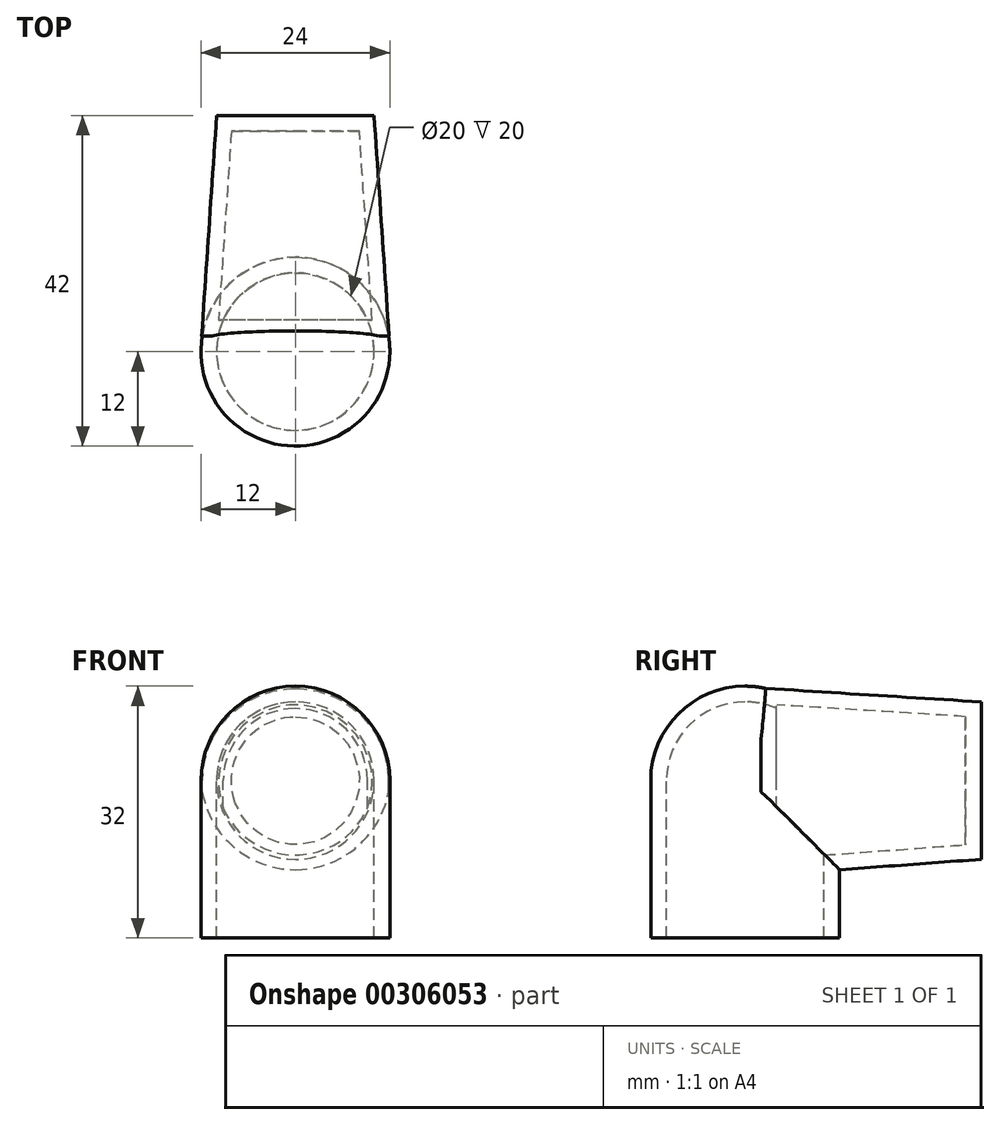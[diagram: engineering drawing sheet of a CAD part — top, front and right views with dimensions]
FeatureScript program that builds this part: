
annotation { "Feature Type Name" : "Feature", "Feature Type Description" : "" }
export const myFeature = defineFeature(function(context is Context, id is Id, definition is map)
    precondition{}
    {
        {
            var Q0;
            Q0=qCreatedBy(makeId("Front.planeOp"),FACE);
            cPlane(context, id + "F0", {"entities" : qUnion([Q0]), "cplaneType" : CPlaneType.OFFSET, "offset" : 28 * mm, "width" : 150 * mm, "height" : 150 * mm});
        }
        {
            var Q0;
            Q0=qCreatedBy(makeId("Front.planeOp"),FACE);
            var sketch = newSketch(context, id + "F1", { "sketchPlane" : qUnion([Q0])});
            skPoint(sketch, "E0", {"position": v(0, 12.5) * mm});
            skPoint(sketch, "E1", {"position": v(0, 27.5) * mm});
            skCircle(sketch, "E2", {"center": v(0, 20) * mm, "radius": 10 * mm});
            skSolve(sketch);
        }
        {
            var Q0;
            Q0=qCreatedBy(makeId("Top.planeOp"),FACE);
            var sketch = newSketch(context, id + "F2", { "sketchPlane" : qUnion([Q0])});
            skCircle(sketch, "E3", {"center": v(0, -30) * mm, "radius": 12 * mm});
            skPoint(sketch, "E4", {"position": v(0, -18) * mm});
            skPoint(sketch, "E5", {"position": v(0, -42) * mm});
            skSolve(sketch);
        }
        {
            var Q0;
            Q0=qCreatedBy(makeId("Right.planeOp"),FACE);
            var sketch = newSketch(context, id + "F3", { "sketchPlane" : qUnion([Q0])});
            skLineSegment(sketch, "E6", {"start": v(-30, 0) * mm, "end": v(-30, 20) * mm});
            skLineSegment(sketch, "E7", {"start": v(-42, 0) * mm, "end": v(-42, 20) * mm});
            skArc(sketch, "E8", {"start": v(-30, 32) * mm, "mid": v(-38.49, 28.49) * mm, "end": v(-42, 20) * mm});
            skLineSegment(sketch, "E9", {"start": v(-30, 32) * mm, "end": v(-30, 20) * mm});
            skLineSegment(sketch, "E10", {"start": v(-30, 0) * mm, "end": v(-42, 0) * mm});
            skSolve(sketch);
        }
        {
            var Q0;
            {var subQ0=sQuery(id+"F3.wireOp",EDGE,"E9");var subQ1=sQuery(id+"F3.wireOp",EDGE,"7151c649-8130-492b-bd59-bcbd0ac8ae9a");var subQ2=makeQuery(id+"F3.imprint","INTERSECT",VERTEX,{"derivedFrom":[subQ1,subQ0]});Q0=makeQuery(id+"F3.imprint","IMPRINT",FACE,{"disambiguationData":[TD([[makeQuery(id+"F3.imprint","IMPRINT",EDGE,{"disambiguationData":[TD([[subQ2,1.0]])],"derivedFrom":subQ1}),1.0]])]});}
            var Q1;
            {var subQ4=sQuery(id+"F3.wireOp",EDGE,"E6");Q1=makeQuery(id+"F3.imprint","IMPRINT",FACE,{"disambiguationData":[TD([[makeQuery(id+"F3.imprint","IMPRINT",EDGE,{"derivedFrom":subQ4}),1.0]])]});}
            var Q2;
            Q2=sQuery(id+"F3.wireOp",EDGE,"E9");
            revolve(context, id + "F4", {"surfaceOperationType" : NewSurfaceOperationType.NEW, "entities" : qUnion([Q0, Q1]), "axis" : qUnion([Q2]), "revolveType" : RevolveType.FULL});
        }
        {
            var Q0;
            Q0=qCreatedBy(id+"F0.planeOp",FACE);
            var sketch = newSketch(context, id + "F5", { "sketchPlane" : qUnion([Q0])});
            skCircle(sketch, "E11", {"center": v(0, 19.85) * mm, "radius": 11.9 * mm});
            skSolve(sketch);
        }
        {
            var Q1;
            Q1=makeQuery(id+"F5.imprint","IMPRINT",FACE,{"disambiguationData":[TD([[makeQuery(id+"F5.imprint","IMPRINT",EDGE,{"derivedFrom":sQuery(id+"F5.wireOp",EDGE,"E11")}),1.0]])]});
            var Q2;
            Q2=makeQuery(id+"F1.imprint","IMPRINT",FACE,{"disambiguationData":[TD([[makeQuery(id+"F1.imprint","IMPRINT",EDGE,{"derivedFrom":sQuery(id+"F1.wireOp",EDGE,"E2")}),1.0]])]});
            loft(context, id + "F6", {"operationType" : NewBodyOperationType.ADD, "sheetProfilesArray" : [{ "sheetProfileEntities" : qUnion([Q1]) }, { "sheetProfileEntities" : qUnion([Q2]) }]});
        }
        {
            var Q0;
            Q0=makeQuery(id+"F4.opRevolve","SWEPT_FACE",FACE,{"disambiguationData":[OSD([sQuery(id+"F3.wireOp",EDGE,"E10")])]});
            var Q1;
            Q1=makeQuery(id+"F6.opLoft","CAP_FACE",FACE,{"disambiguationData":[OSD([makeQuery(id+"F1.imprint","IMPRINT",FACE,{"disambiguationData":[TD([[makeQuery(id+"F1.imprint","IMPRINT",EDGE,{"derivedFrom":sQuery(id+"F1.wireOp",EDGE,"E2")}),1.0]])]})])],"isStart":true});
            shell(context, id + "F7", {"entities" : qUnion([Q0, Q1]), "thickness" : 2 * mm});
        }
    });
